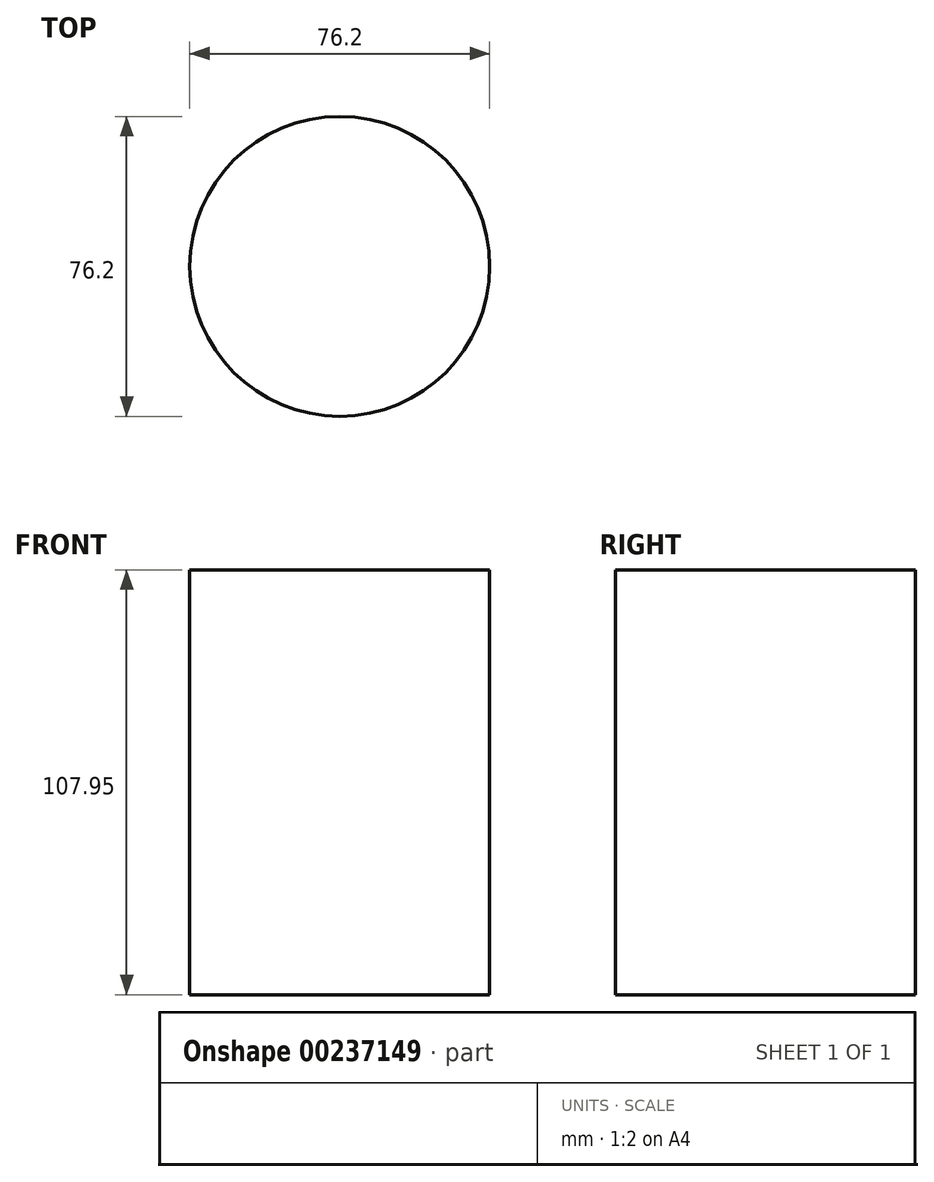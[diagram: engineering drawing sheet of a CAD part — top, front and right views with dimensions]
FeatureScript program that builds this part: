
annotation { "Feature Type Name" : "Feature", "Feature Type Description" : "" }
export const myFeature = defineFeature(function(context is Context, id is Id, definition is map)
    precondition{}
    {
        {
            var Q0;
            Q0=qCreatedBy(makeId("Top.planeOp"),FACE);
            var sketch = newSketch(context, id + "F0", { "sketchPlane" : qUnion([Q0])});
            skCircle(sketch, "E0", {"center": v(0, 0) * mm, "radius": 38.1 * mm});
            skSolve(sketch);
        }
        {
            var Q0;
            Q0=makeQuery(id+"F0.imprint","IMPRINT",FACE,{"disambiguationData":[TD([[makeQuery(id+"F0.imprint","IMPRINT",EDGE,{"derivedFrom":sQuery(id+"F0.wireOp",EDGE,"E0")}),1.0]])]});
            extrude(context, id + "F1", {"entities" : qUnion([Q0]), "depth" : 107.95 * mm});
        }
    });
